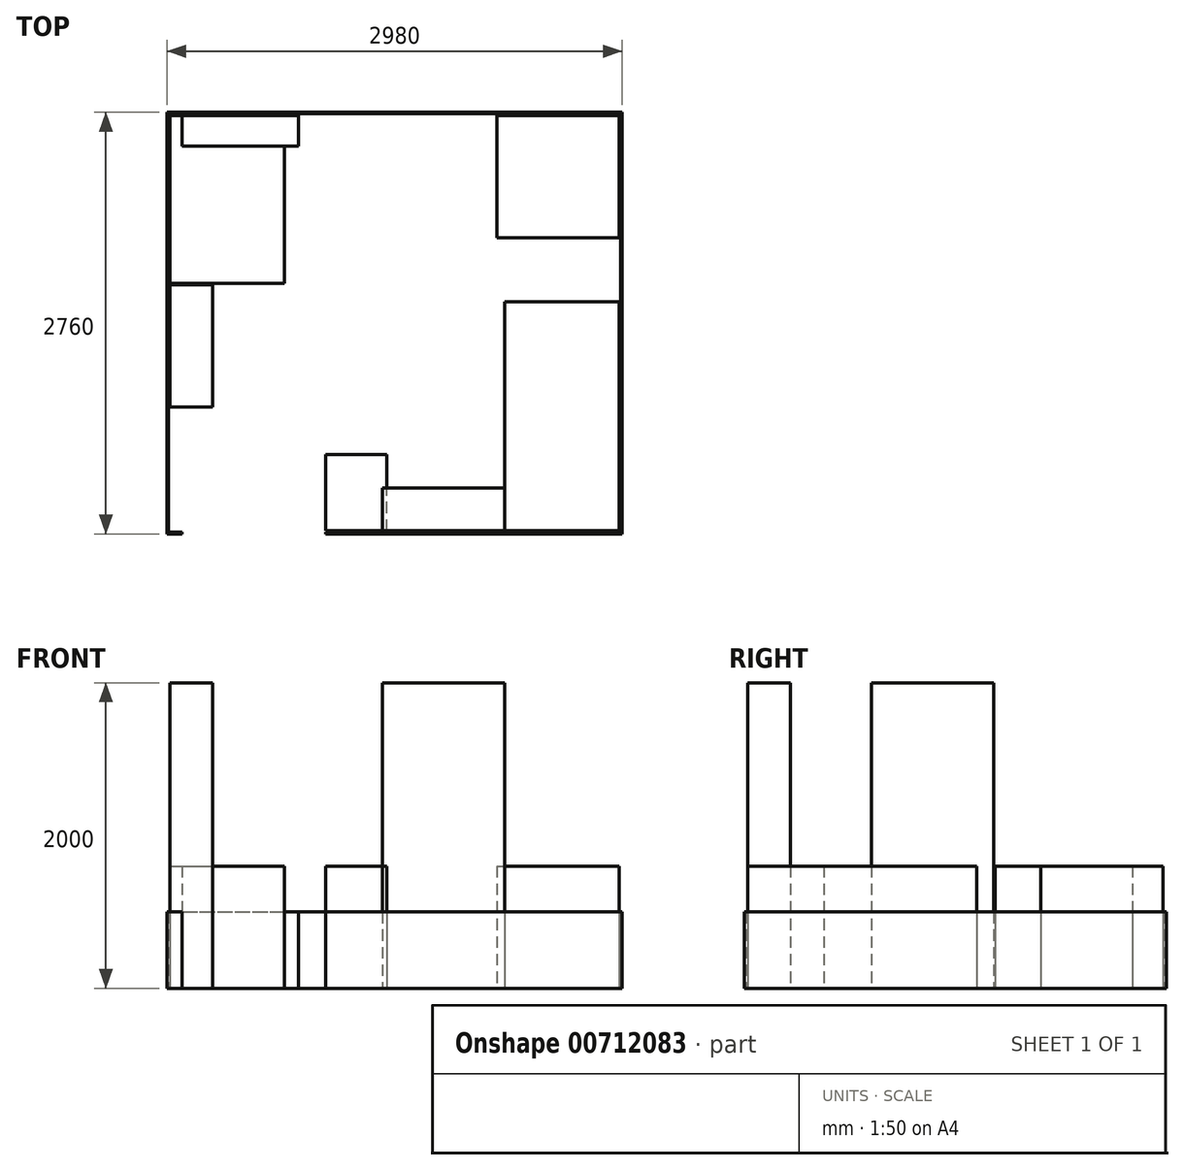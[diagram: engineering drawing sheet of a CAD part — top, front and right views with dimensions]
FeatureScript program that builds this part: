
annotation { "Feature Type Name" : "Feature", "Feature Type Description" : "" }
export const myFeature = defineFeature(function(context is Context, id is Id, definition is map)
    precondition{}
    {
        {
            var Q0;
            Q0=qCreatedBy(makeId("Top.planeOp"),FACE);
            var sketch = newSketch(context, id + "F0", { "sketchPlane" : qUnion([Q0])});
            skLineSegment(sketch, "E0.bottom", {"start": v(-1490, 1990) * mm, "end": v(1470, 1990) * mm});
            skLineSegment(sketch, "E0.top", {"start": v(-1490, -750) * mm, "end": v(-1400, -750) * mm});
            skLineSegment(sketch, "E0.left", {"start": v(-1490, 1990) * mm, "end": v(-1490, -750) * mm});
            skLineSegment(sketch, "E0.right", {"start": v(1470, 1990) * mm, "end": v(1470, -750) * mm});
            skLineSegment(sketch, "E1.0", {"start": v(-1500, 2000) * mm, "end": v(-1500, -760) * mm});
            skLineSegment(sketch, "E1.1", {"start": v(-1500, 2000) * mm, "end": v(1480, 2000) * mm});
            skLineSegment(sketch, "E1.2", {"start": v(1480, 2000) * mm, "end": v(1480, -760) * mm});
            skLineSegment(sketch, "E1.3", {"start": v(-1500, -760) * mm, "end": v(-1400, -760) * mm});
            skLineSegment(sketch, "E2", {"start": v(-1400, -750) * mm, "end": v(-1400, -760) * mm});
            skLineSegment(sketch, "E3", {"start": v(-460, -750) * mm, "end": v(-460, -760) * mm});
            skLineSegment(sketch, "E4.trimOffspring", {"start": v(-460, -750) * mm, "end": v(1470, -750) * mm});
            skLineSegment(sketch, "E5.trimOffspring", {"start": v(-460, -760) * mm, "end": v(1480, -760) * mm});
            skLineSegment(sketch, "E6.bottom", {"start": v(710, 760) * mm, "end": v(1460, 760) * mm});
            skLineSegment(sketch, "E6.top", {"start": v(710, -740) * mm, "end": v(1460, -740) * mm});
            skLineSegment(sketch, "E6.left", {"start": v(710, 760) * mm, "end": v(710, -740) * mm});
            skLineSegment(sketch, "E6.right", {"start": v(1460, 760) * mm, "end": v(1460, -740) * mm});
            skLineSegment(sketch, "E7.bottom", {"start": v(-1480, 70) * mm, "end": v(-1200, 70) * mm});
            skLineSegment(sketch, "E7.top", {"start": v(-1480, 870) * mm, "end": v(-1200, 870) * mm});
            skLineSegment(sketch, "E7.left", {"start": v(-1480, 70) * mm, "end": v(-1480, 870) * mm});
            skLineSegment(sketch, "E7.right", {"start": v(-1200, 70) * mm, "end": v(-1200, 870) * mm});
            skLineSegment(sketch, "E8.bottom", {"start": v(660, 1980) * mm, "end": v(1460, 1980) * mm});
            skLineSegment(sketch, "E8.top", {"start": v(660, 1180) * mm, "end": v(1460, 1180) * mm});
            skLineSegment(sketch, "E8.left", {"start": v(660, 1980) * mm, "end": v(660, 1180) * mm});
            skLineSegment(sketch, "E8.right", {"start": v(1460, 1980) * mm, "end": v(1460, 1180) * mm});
            skLineSegment(sketch, "E9.bottom", {"start": v(-90, -740) * mm, "end": v(710, -740) * mm});
            skLineSegment(sketch, "E9.top", {"start": v(-90, -460) * mm, "end": v(710, -460) * mm});
            skLineSegment(sketch, "E9.left", {"start": v(-90, -740) * mm, "end": v(-90, -460) * mm});
            skLineSegment(sketch, "E9.right", {"start": v(710, -740) * mm, "end": v(710, -460) * mm});
            skLineSegment(sketch, "E10.bottom", {"start": v(-1400, 1980) * mm, "end": v(-640, 1980) * mm});
            skLineSegment(sketch, "E10.top", {"start": v(-1400, 1780) * mm, "end": v(-640, 1780) * mm});
            skLineSegment(sketch, "E10.left", {"start": v(-1400, 1980) * mm, "end": v(-1400, 1780) * mm});
            skLineSegment(sketch, "E10.right", {"start": v(-640, 1980) * mm, "end": v(-640, 1780) * mm});
            skLineSegment(sketch, "E11.bottom", {"start": v(-1480, 1980) * mm, "end": v(-730, 1980) * mm});
            skLineSegment(sketch, "E11.top", {"start": v(-1480, 880) * mm, "end": v(-730, 880) * mm});
            skLineSegment(sketch, "E11.left", {"start": v(-1480, 1980) * mm, "end": v(-1480, 880) * mm});
            skLineSegment(sketch, "E11.right", {"start": v(-730, 1980) * mm, "end": v(-730, 880) * mm});
            skLineSegment(sketch, "E12.bottom", {"start": v(-460, -740) * mm, "end": v(-60, -740) * mm});
            skLineSegment(sketch, "E12.top", {"start": v(-460, -240) * mm, "end": v(-60, -240) * mm});
            skLineSegment(sketch, "E12.left", {"start": v(-460, -740) * mm, "end": v(-460, -240) * mm});
            skLineSegment(sketch, "E12.right", {"start": v(-60, -740) * mm, "end": v(-60, -240) * mm});
            skSolve(sketch);
        }
        {
            var Q0;
            Q0=makeQuery(id+"F0.imprint","IMPRINT",FACE,{"disambiguationData":[TD([[makeQuery(id+"F0.imprint","IMPRINT",EDGE,{"derivedFrom":sQuery(id+"F0.wireOp",EDGE,"E0.bottom")}),1.0]])]});
            extrude(context, id + "F1", {"entities" : qUnion([Q0]), "depth" : 500 * mm, "offsetDistance" : 25 * mm});
        }
        {
            var Q0;
            Q0=makeQuery(id+"F0.imprint","IMPRINT",FACE,{"disambiguationData":[TD([[makeQuery(id+"F0.imprint","IMPRINT",EDGE,{"derivedFrom":sQuery(id+"F0.wireOp",EDGE,"E7.bottom")}),1.0]])]});
            extrude(context, id + "F2", {"entities" : qUnion([Q0]), "depth" : 2000 * mm, "offsetDistance" : 25 * mm});
        }
        {
            var Q0;
            Q0=makeQuery(id+"F0.imprint","IMPRINT",FACE,{"disambiguationData":[TD([[makeQuery(id+"F0.imprint","IMPRINT",EDGE,{"derivedFrom":sQuery(id+"F0.wireOp",EDGE,"E10.bottom")}),-1.0]])]});
            extrude(context, id + "F3", {"entities" : qUnion([Q0]), "depth" : 500 * mm, "offsetDistance" : 25 * mm});
        }
        {
            var Q0;
            Q0=makeQuery(id+"F0.imprint","IMPRINT",FACE,{"disambiguationData":[TD([[makeQuery(id+"F0.imprint","IMPRINT",EDGE,{"derivedFrom":sQuery(id+"F0.wireOp",EDGE,"E11.bottom")}),-1.0]])]});
            var Q1;
            {var subQ2=sQuery(id+"F0.wireOp",EDGE,"E10.left");Q1=makeQuery(id+"F0.imprint","IMPRINT",FACE,{"disambiguationData":[TD([[makeQuery(id+"F0.imprint","IMPRINT",EDGE,{"derivedFrom":subQ2}),-1.0]])]});}
            extrude(context, id + "F4", {"entities" : qUnion([Q0, Q1]), "depth" : 800 * mm, "offsetDistance" : 25 * mm});
        }
        {
            var Q0;
            Q0=makeQuery(id+"F0.imprint","IMPRINT",FACE,{"disambiguationData":[TD([[makeQuery(id+"F0.imprint","IMPRINT",EDGE,{"derivedFrom":sQuery(id+"F0.wireOp",EDGE,"E9.bottom")}),1.0]])]});
            extrude(context, id + "F5", {"entities" : qUnion([Q0]), "depth" : 2000 * mm, "offsetDistance" : 25 * mm});
        }
        {
            var Q0;
            Q0=makeQuery(id+"F0.imprint","IMPRINT",FACE,{"disambiguationData":[TD([[makeQuery(id+"F0.imprint","IMPRINT",EDGE,{"derivedFrom":sQuery(id+"F0.wireOp",EDGE,"E6.bottom")}),-1.0]])]});
            extrude(context, id + "F6", {"entities" : qUnion([Q0]), "depth" : 800 * mm, "offsetDistance" : 25 * mm});
        }
        {
            var Q0;
            Q0=makeQuery(id+"F0.imprint","IMPRINT",FACE,{"disambiguationData":[TD([[makeQuery(id+"F0.imprint","IMPRINT",EDGE,{"derivedFrom":sQuery(id+"F0.wireOp",EDGE,"E8.bottom")}),-1.0]])]});
            extrude(context, id + "F7", {"entities" : qUnion([Q0]), "depth" : 800 * mm, "offsetDistance" : 25 * mm});
        }
        {
            var Q0;
            {var subQ1=sQuery(id+"F0.wireOp",EDGE,"E9.left");Q0=makeQuery(id+"F0.imprint","IMPRINT",FACE,{"disambiguationData":[TD([[makeQuery(id+"F0.imprint","IMPRINT",EDGE,{"derivedFrom":subQ1}),1.0]])]});}
            var Q1;
            {var subQ0=sQuery(id+"F0.wireOp",EDGE,"E9.left");Q1=makeQuery(id+"F0.imprint","IMPRINT",FACE,{"disambiguationData":[TD([[makeQuery(id+"F0.imprint","IMPRINT",EDGE,{"derivedFrom":subQ0}),-1.0]])]});}
            extrude(context, id + "F8", {"entities" : qUnion([Q0, Q1]), "depth" : 800 * mm, "offsetDistance" : 25 * mm});
        }
    });
